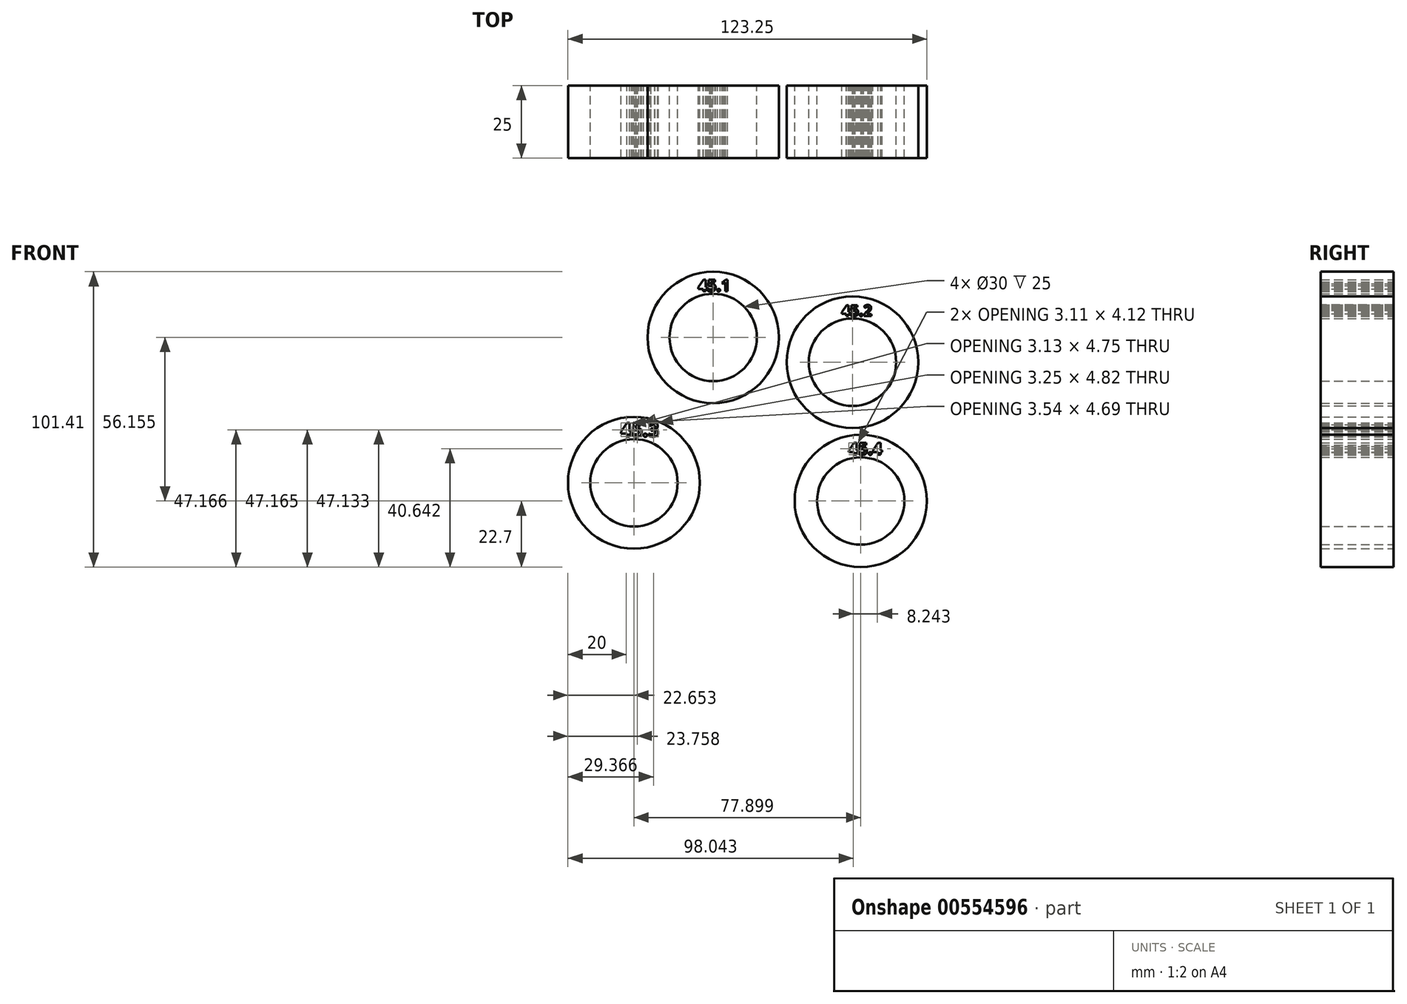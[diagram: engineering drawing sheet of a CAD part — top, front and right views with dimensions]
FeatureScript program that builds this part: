
annotation { "Feature Type Name" : "Feature", "Feature Type Description" : "" }
export const myFeature = defineFeature(function(context is Context, id is Id, definition is map)
    precondition{}
    {
        {
            var Q0;
            Q0=qCreatedBy(makeId("Front.planeOp"),FACE);
            var sketch = newSketch(context, id + "F0", { "sketchPlane" : qUnion([Q0])});
            skCircle(sketch, "E0", {"center": v(-46.6, -19.38) * mm, "radius": 22.65 * mm});
            skCircle(sketch, "E1", {"center": v(-46.6, -19.38) * mm, "radius": 15 * mm});
            skText(sketch, "E2", { "text": "45.3", "fontName": "OpenSans-Bold.ttf"});
            skCircle(sketch, "E3", {"center": v(31.3, -25.62) * mm, "radius": 22.7 * mm});
            skCircle(sketch, "E4", {"center": v(31.3, -25.62) * mm, "radius": 15 * mm});
            skText(sketch, "E5", { "text": "45.4", "fontName": "OpenSans-Bold.ttf"});
            skCircle(sketch, "E6", {"center": v(28.46, 22.03) * mm, "radius": 22.6 * mm});
            skCircle(sketch, "E7", {"center": v(28.46, 22.03) * mm, "radius": 15 * mm});
            skText(sketch, "E8", { "text": "45.2", "fontName": "OpenSans-Bold.ttf"});
            skCircle(sketch, "E9", {"center": v(-19.38, 30.54) * mm, "radius": 22.55 * mm});
            skCircle(sketch, "E10", {"center": v(-19.38, 30.54) * mm, "radius": 15 * mm});
            skText(sketch, "E11", { "text": "45.1\n", "fontName": "OpenSans-Bold.ttf"});
            const initialGuessF0  = {"E2": [-0.05114, -0.0035, 1, 0, 0.00473], "E5": [0.02713, -0.00974, 1, 0, 0.00416], "E8": [0.02467, 0.0379, 1, 0, 0.00378], "E11": [-0.02456, 0.04637, 1, 0, 0.00397]};
            skSetInitialGuess(sketch, initialGuessF0);
            skSolve(sketch);
        }
        {
            var Q0;
            Q0=makeQuery(id+"F0.imprint","IMPRINT",FACE,{"disambiguationData":[TD([[makeQuery(id+"F0.imprint","IMPRINT",EDGE,{"derivedFrom":sQuery(id+"F0.wireOp",EDGE,"E0")}),1.0]])]});
            extrude(context, id + "F1", {"entities" : qUnion([Q0]), "depth" : 25 * mm, "offsetDistance" : 25 * mm});
        }
        {
            var Q0;
            Q0 = qSketchRegion(id + "F0", true);
            extrude(context, id + "F2", {"entities" : qUnion([Q0]), "operationType" : NewBodyOperationType.ADD, "depth" : 25 * mm, "offsetDistance" : 25 * mm});
        }
    });
